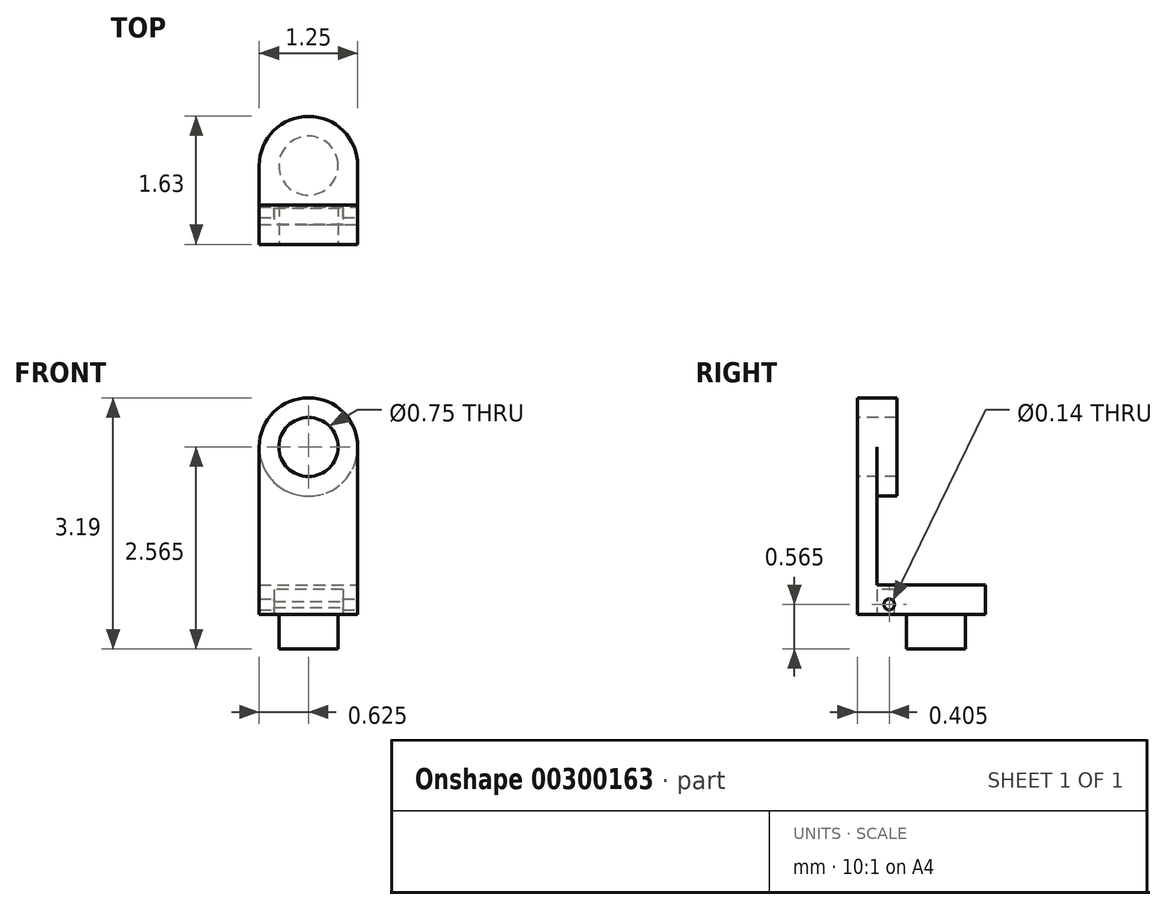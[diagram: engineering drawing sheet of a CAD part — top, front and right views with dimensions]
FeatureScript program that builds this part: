
annotation { "Feature Type Name" : "Feature", "Feature Type Description" : "" }
export const myFeature = defineFeature(function(context is Context, id is Id, definition is map)
    precondition{}
    {
        {
            var Q0;
            Q0=qCreatedBy(makeId("Front.planeOp"),FACE);
            var sketch = newSketch(context, id + "F0", { "sketchPlane" : qUnion([Q0])});
            skLineSegment(sketch, "E0.bottom", {"start": v(0, 0) * mm, "end": v(1.25, 0) * mm});
            skLineSegment(sketch, "E0.top", {"start": v(0, 2.12) * mm, "end": v(1.25, 2.12) * mm});
            skLineSegment(sketch, "E0.left", {"start": v(0, 0) * mm, "end": v(0, 2.12) * mm});
            skLineSegment(sketch, "E0.right", {"start": v(1.25, 0) * mm, "end": v(1.25, 2.12) * mm});
            skSolve(sketch);
        }
        {
            var Q0;
            Q0=makeQuery(id+"F0.imprint","IMPRINT",FACE,{"disambiguationData":[TD([[makeQuery(id+"F0.imprint","IMPRINT",EDGE,{"derivedFrom":sQuery(id+"F0.wireOp",EDGE,"E0.bottom")}),1.0]])]});
            extrude(context, id + "F1", {"entities" : qUnion([Q0]), "depth" : 0.25 * mm});
        }
        {
            var Q0;
            Q0=makeQuery(id+"F1.opExtrude","CAP_FACE",FACE,{"disambiguationData":[OSD([sQuery(id+"F0.wireOp",EDGE,"E0.bottom"),sQuery(id+"F0.wireOp",EDGE,"E0.top"),sQuery(id+"F0.wireOp",EDGE,"E0.left"),sQuery(id+"F0.wireOp",EDGE,"E0.right")])],"isStart":false});
            var sketch = newSketch(context, id + "F2", { "sketchPlane" : qUnion([Q0])});
            skCircle(sketch, "E1", {"center": v(0.62, 2.13) * mm, "radius": 0.62 * mm});
            skCircle(sketch, "E2", {"center": v(0.62, 2.13) * mm, "radius": 0.38 * mm});
            skSolve(sketch);
        }
        {
            var Q0;
            {var subQ1=makeQuery(id+"F1.opExtrude","CAP_EDGE",EDGE,{"disambiguationData":[OSD([sQuery(id+"F0.wireOp",EDGE,"E0.top")])],"isStart":false});var subQ4=sQuery(id+"F2.wireOp",EDGE,"E2");var subQ5=makeQuery(id+"F2.imprint","INTERSECT",VERTEX,{"disambiguationData":[OD(0.0)],"derivedFrom":[subQ1,subQ4]});Q0=makeQuery(id+"F2.imprint","IMPRINT",FACE,{"disambiguationData":[TD([[makeQuery(id+"F2.imprint","IMPRINT",EDGE,{"disambiguationData":[TD([[subQ5,-1.0]])],"derivedFrom":subQ4}),-1.0]])]});}
            var Q1;
            {var subQ1=makeQuery(id+"F1.opExtrude","CAP_EDGE",EDGE,{"disambiguationData":[OSD([sQuery(id+"F0.wireOp",EDGE,"E0.top")])],"isStart":false});var subQ4=sQuery(id+"F2.wireOp",EDGE,"E2");var subQ5=makeQuery(id+"F2.imprint","INTERSECT",VERTEX,{"disambiguationData":[OD(0.0)],"derivedFrom":[subQ1,subQ4]});Q1=makeQuery(id+"F2.imprint","IMPRINT",FACE,{"disambiguationData":[TD([[makeQuery(id+"F2.imprint","IMPRINT",EDGE,{"disambiguationData":[TD([[subQ5,1.0]])],"derivedFrom":subQ4}),-1.0]])]});}
            extrude(context, id + "F3", {"entities" : qUnion([Q0, Q1]), "operationType" : NewBodyOperationType.ADD, "oppositeDirection" : true, "depth" : 0.5 * mm});
        }
        {
            var Q0;
            {var subQ0=sQuery(id+"F0.wireOp",EDGE,"E0.top");Q0=makeQuery(id+"F3.boolean.opBoolean","SPLIT",FACE,{"disambiguationData":[TD([makeQuery(id+"F1.opExtrude","SWEPT_FACE",FACE,{"disambiguationData":[OSD([subQ0])]})])],"derivedFrom":makeQuery(id+"F1.opExtrude","CAP_FACE",FACE,{"disambiguationData":[OSD([sQuery(id+"F0.wireOp",EDGE,"E0.bottom"),subQ0,sQuery(id+"F0.wireOp",EDGE,"E0.left"),sQuery(id+"F0.wireOp",EDGE,"E0.right")])],"isStart":true})});}
            var sketch = newSketch(context, id + "F4", { "sketchPlane" : qUnion([Q0])});
            skArc(sketch, "E3.0.0", {"start": v(-1, 2.13) * mm, "mid": v(-0.62, 1.75) * mm, "end": v(-0.25, 2.13) * mm});
            skLineSegment(sketch, "E3.0.1", {"start": v(-0.25, 2.12) * mm, "end": v(-1, 2.12) * mm});
            skSolve(sketch);
        }
        {
            var Q0;
            Q0 = qSketchRegion(id + "F4", true);
            extrude(context, id + "F5", {"entities" : qUnion([Q0]), "operationType" : NewBodyOperationType.REMOVE, "oppositeDirection" : true, "depth" : 25 * mm});
        }
        {
            var Q0;
            Q0=makeQuery(id+"F1.opExtrude","SWEPT_FACE",FACE,{"disambiguationData":[OSD([sQuery(id+"F0.wireOp",EDGE,"E0.bottom")])]});
            var sketch = newSketch(context, id + "F6", { "sketchPlane" : qUnion([Q0])});
            skLineSegment(sketch, "E4.bottom", {"start": v(1.25, 0.25) * mm, "end": v(0, 0.25) * mm});
            skLineSegment(sketch, "E4.left", {"start": v(1.25, 0.25) * mm, "end": v(1.25, -0.75) * mm});
            skLineSegment(sketch, "E4.right", {"start": v(0, 0.25) * mm, "end": v(0, -0.75) * mm});
            skArc(sketch, "E5", {"start": v(0, -0.75) * mm, "mid": v(0.63, -1.38) * mm, "end": v(1.25, -0.75) * mm});
            skSolve(sketch);
        }
        {
            var Q0;
            Q0 = qSketchRegion(id + "F6", true);
            extrude(context, id + "F7", {"entities" : qUnion([Q0]), "operationType" : NewBodyOperationType.ADD, "oppositeDirection" : true, "depth" : 0.38 * mm});
        }
        {
            var Q0;
            Q0=makeQuery(id+"F7.boolean.opBoolean","MERGE",FACE,{"derivedFrom":[makeQuery(id+"F1.opExtrude","SWEPT_FACE",FACE,{"disambiguationData":[OSD([sQuery(id+"F0.wireOp",EDGE,"E0.bottom")])]}),makeQuery(id+"F7.opExtrude","CAP_FACE",FACE,{"disambiguationData":[OSD([sQuery(id+"F6.wireOp",EDGE,"E4.bottom"),sQuery(id+"F6.wireOp",EDGE,"E4.left"),sQuery(id+"F6.wireOp",EDGE,"E4.right"),sQuery(id+"F6.wireOp",EDGE,"E5")])],"isStart":true})]});
            var sketch = newSketch(context, id + "F8", { "sketchPlane" : qUnion([Q0])});
            skArc(sketch, "E6.0", {"start": v(0, -0.75) * mm, "mid": v(0.63, -1.38) * mm, "end": v(1.25, -0.75) * mm});
            skCircle(sketch, "E7", {"center": v(0.63, -0.75) * mm, "radius": 0.38 * mm});
            skSolve(sketch);
        }
        {
            var Q0;
            Q0=makeQuery(id+"F8.imprint","IMPRINT",FACE,{"disambiguationData":[TD([[makeQuery(id+"F8.imprint","IMPRINT",EDGE,{"derivedFrom":sQuery(id+"F8.wireOp",EDGE,"E7")}),1.0]])]});
            extrude(context, id + "F9", {"entities" : qUnion([Q0]), "operationType" : NewBodyOperationType.ADD, "depth" : 0.44 * mm});
        }
        {
            var Q0;
            Q0=makeQuery(id+"F7.boolean.opBoolean","MERGE",FACE,{"derivedFrom":[makeQuery(id+"F1.opExtrude","SWEPT_FACE",FACE,{"disambiguationData":[OSD([sQuery(id+"F0.wireOp",EDGE,"E0.bottom")])]}),makeQuery(id+"F7.opExtrude","CAP_FACE",FACE,{"disambiguationData":[OSD([sQuery(id+"F6.wireOp",EDGE,"E4.bottom"),sQuery(id+"F6.wireOp",EDGE,"E4.left"),sQuery(id+"F6.wireOp",EDGE,"E4.right"),sQuery(id+"F6.wireOp",EDGE,"E5")])],"isStart":true})]});
            var sketch = newSketch(context, id + "F10", { "sketchPlane" : qUnion([Q0])});
            skLineSegment(sketch, "E8.bottom", {"start": v(1.06, -0.21) * mm, "end": v(0.19, -0.21) * mm});
            skLineSegment(sketch, "E8.top", {"start": v(1.06, 0) * mm, "end": v(0.19, 0) * mm});
            skLineSegment(sketch, "E8.left", {"start": v(1.06, -0.21) * mm, "end": v(1.06, 0) * mm});
            skLineSegment(sketch, "E8.right", {"start": v(0.19, -0.21) * mm, "end": v(0.19, 0) * mm});
            skSolve(sketch);
        }
        {
            var Q0;
            Q0=makeQuery(id+"F10.imprint","IMPRINT",FACE,{"disambiguationData":[TD([[makeQuery(id+"F10.imprint","IMPRINT",EDGE,{"derivedFrom":sQuery(id+"F10.wireOp",EDGE,"E8.bottom")}),-1.0]])]});
            extrude(context, id + "F11", {"entities" : qUnion([Q0]), "operationType" : NewBodyOperationType.REMOVE, "oppositeDirection" : true, "depth" : 0.32 * mm});
        }
        {
            var Q0;
            Q0=makeQuery(id+"F7.boolean.opBoolean","MERGE",FACE,{"derivedFrom":[makeQuery(id+"F1.opExtrude","SWEPT_FACE",FACE,{"disambiguationData":[OSD([sQuery(id+"F0.wireOp",EDGE,"E0.right")])]}),makeQuery(id+"F7.opExtrude","SWEPT_FACE",FACE,{"disambiguationData":[OSD([sQuery(id+"F6.wireOp",EDGE,"E4.left")])]})]});
            var sketch = newSketch(context, id + "F12", { "sketchPlane" : qUnion([Q0])});
            skCircle(sketch, "E9", {"center": v(0.16, 0.12) * mm, "radius": 0.07 * mm});
            skSolve(sketch);
        }
        {
            var Q0;
            Q0=makeQuery(id+"F12.imprint","IMPRINT",FACE,{"disambiguationData":[TD([[makeQuery(id+"F12.imprint","IMPRINT",EDGE,{"derivedFrom":sQuery(id+"F12.wireOp",EDGE,"E9")}),1.0]])]});
            extrude(context, id + "F13", {"entities" : qUnion([Q0]), "operationType" : NewBodyOperationType.REMOVE, "endBound" : BoundingType.THROUGH_ALL, "oppositeDirection" : true, "depth" : 25 * mm});
        }
    });
